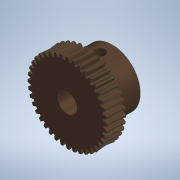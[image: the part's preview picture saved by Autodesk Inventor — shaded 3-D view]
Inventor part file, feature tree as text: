
AUTODESK INVENTOR PART (.ipt)
format: ipt  version: 2022 (Build 260153000, 153)  size: 2,117,632 bytes
history: mixed  units: in
note: dims shown in document units (in); Inventor stores cm internally (conversion verified against a paired STEP export)
features: hole x1, sketch x1, imported_body x1
ambient origin geometry x8: Origin, YZ Plane, XZ Plane, XY Plane, X Axis, Y Axis, Z Axis, Center Point
bodies: Solid1 (imported_parasolid), Body1 (imported_parasolid)
feature tree (3):
  hole  "Hole1"  [1 undecoded]
  sketch  "Sketch1"  dims[d0=0.1969in d1=0.2362in d2=0.1575in d3=0.0787in d4=90.0deg d5=0.315in d6=0.8108in]
  imported_body  NMx_Import_Brep_tag  [imported B-rep: ~5 faces, bbox_mm=None]
note: 1 required parameter value undecoded (feature->parameter linkage not recoverable at this tier; creation-order binding heuristic only, values carry confidence <= 0.55)
